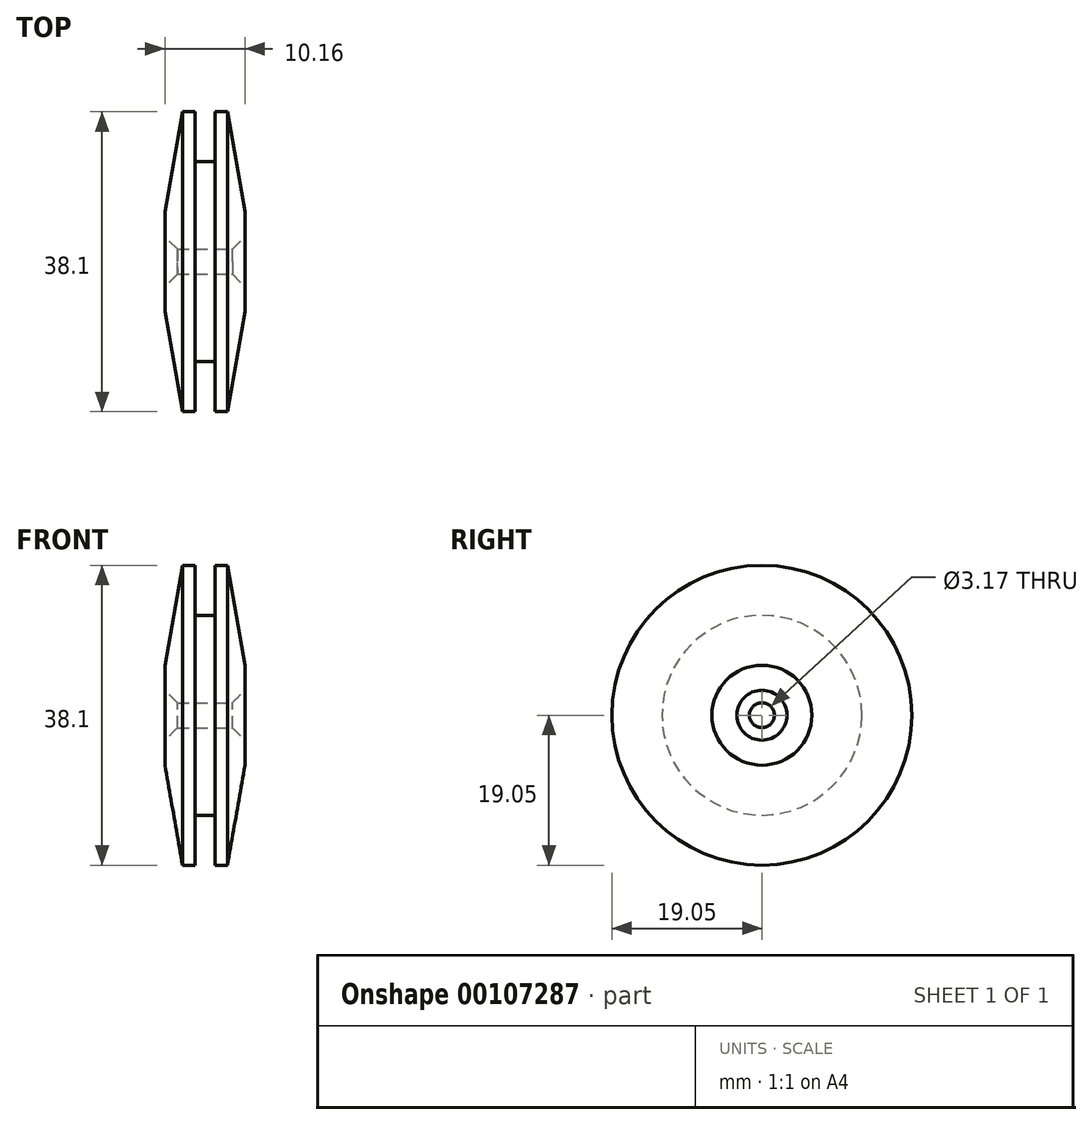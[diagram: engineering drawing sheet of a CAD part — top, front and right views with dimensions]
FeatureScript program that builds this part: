
annotation { "Feature Type Name" : "Feature", "Feature Type Description" : "" }
export const myFeature = defineFeature(function(context is Context, id is Id, definition is map)
    precondition{}
    {
        {
            var Q0;
            Q0=qCreatedBy(makeId("Front.planeOp"),FACE);
            var sketch = newSketch(context, id + "F0", { "sketchPlane" : qUnion([Q0])});
            skLineSegment(sketch, "E0", {"start": v(0, 12.7) * mm, "end": v(-1.27, 12.7) * mm});
            skLineSegment(sketch, "E1", {"start": v(-1.27, 12.7) * mm, "end": v(-1.27, 19.05) * mm});
            skLineSegment(sketch, "E2", {"start": v(1.27, 19.05) * mm, "end": v(1.27, 12.7) * mm});
            skLineSegment(sketch, "E3", {"start": v(1.27, 12.7) * mm, "end": v(0, 12.7) * mm});
            skLineSegment(sketch, "E4", {"start": v(5.08, 6.35) * mm, "end": v(5.08, 0) * mm});
            skLineSegment(sketch, "E5", {"start": v(5.08, 0) * mm, "end": v(-5.08, 0) * mm});
            skLineSegment(sketch, "E6", {"start": v(-5.08, 0) * mm, "end": v(-5.08, 6.35) * mm});
            skLineSegment(sketch, "E7", {"start": v(1.27, 19.05) * mm, "end": v(2.86, 19.05) * mm});
            skLineSegment(sketch, "E8", {"start": v(2.86, 19.05) * mm, "end": v(5.08, 6.35) * mm});
            skLineSegment(sketch, "E9", {"start": v(-1.27, 19.05) * mm, "end": v(-2.86, 19.05) * mm});
            skLineSegment(sketch, "E10", {"start": v(-2.86, 19.05) * mm, "end": v(-5.08, 6.35) * mm});
            skSolve(sketch);
        }
        {
            var Q0;
            Q0=makeQuery(id+"F0.imprint","IMPRINT",FACE,{"disambiguationData":[TD([[makeQuery(id+"F0.imprint","IMPRINT",EDGE,{"derivedFrom":sQuery(id+"F0.wireOp",EDGE,"E0")}),1.0]])]});
            var Q1;
            Q1=sQuery(id+"F0.wireOp",EDGE,"E5");
            revolve(context, id + "F1", {"entities" : qUnion([Q0]), "axis" : qUnion([Q1]), "revolveType" : RevolveType.FULL});
        }
        {
            var Q0;
            Q0=qCreatedBy(makeId("Right.planeOp"),FACE);
            var sketch = newSketch(context, id + "F2", { "sketchPlane" : qUnion([Q0])});
            skCircle(sketch, "E11", {"center": v(0, 0) * mm, "radius": 1.59 * mm});
            skSolve(sketch);
        }
        {
            var Q0;
            Q0=qSketchRegion(id+"F2",true);
            extrude(context, id + "F3", {"entities" : qUnion([Q0]), "operationType" : NewBodyOperationType.REMOVE, "endBound" : BoundingType.SYMMETRIC, "oppositeDirection" : true, "depth" : 25.4 * mm});
        }
        {
            var Q0;
            Q0=makeQuery(id+"F3.boolean.opBoolean","INTERSECT",EDGE,{"derivedFrom":[makeQuery(id+"F1.opRevolve","SWEPT_FACE",FACE,{"disambiguationData":[OSD([sQuery(id+"F0.wireOp",EDGE,"E4")])]}),makeQuery(id+"F3.opExtrude","SWEPT_FACE",FACE,{"disambiguationData":[OSD([sQuery(id+"F2.wireOp",EDGE,"E11")])]})]});
            var Q1;
            Q1=makeQuery(id+"F3.boolean.opBoolean","INTERSECT",EDGE,{"derivedFrom":[makeQuery(id+"F1.opRevolve","SWEPT_FACE",FACE,{"disambiguationData":[OSD([sQuery(id+"F0.wireOp",EDGE,"E6")])]}),makeQuery(id+"F3.opExtrude","SWEPT_FACE",FACE,{"disambiguationData":[OSD([sQuery(id+"F2.wireOp",EDGE,"E11")])]})]});
            chamfer(context, id + "F4", {"entities" : qUnion([Q0, Q1]), "width" : 1.59 * mm, "tangentPropagation" : true});
        }
    });
